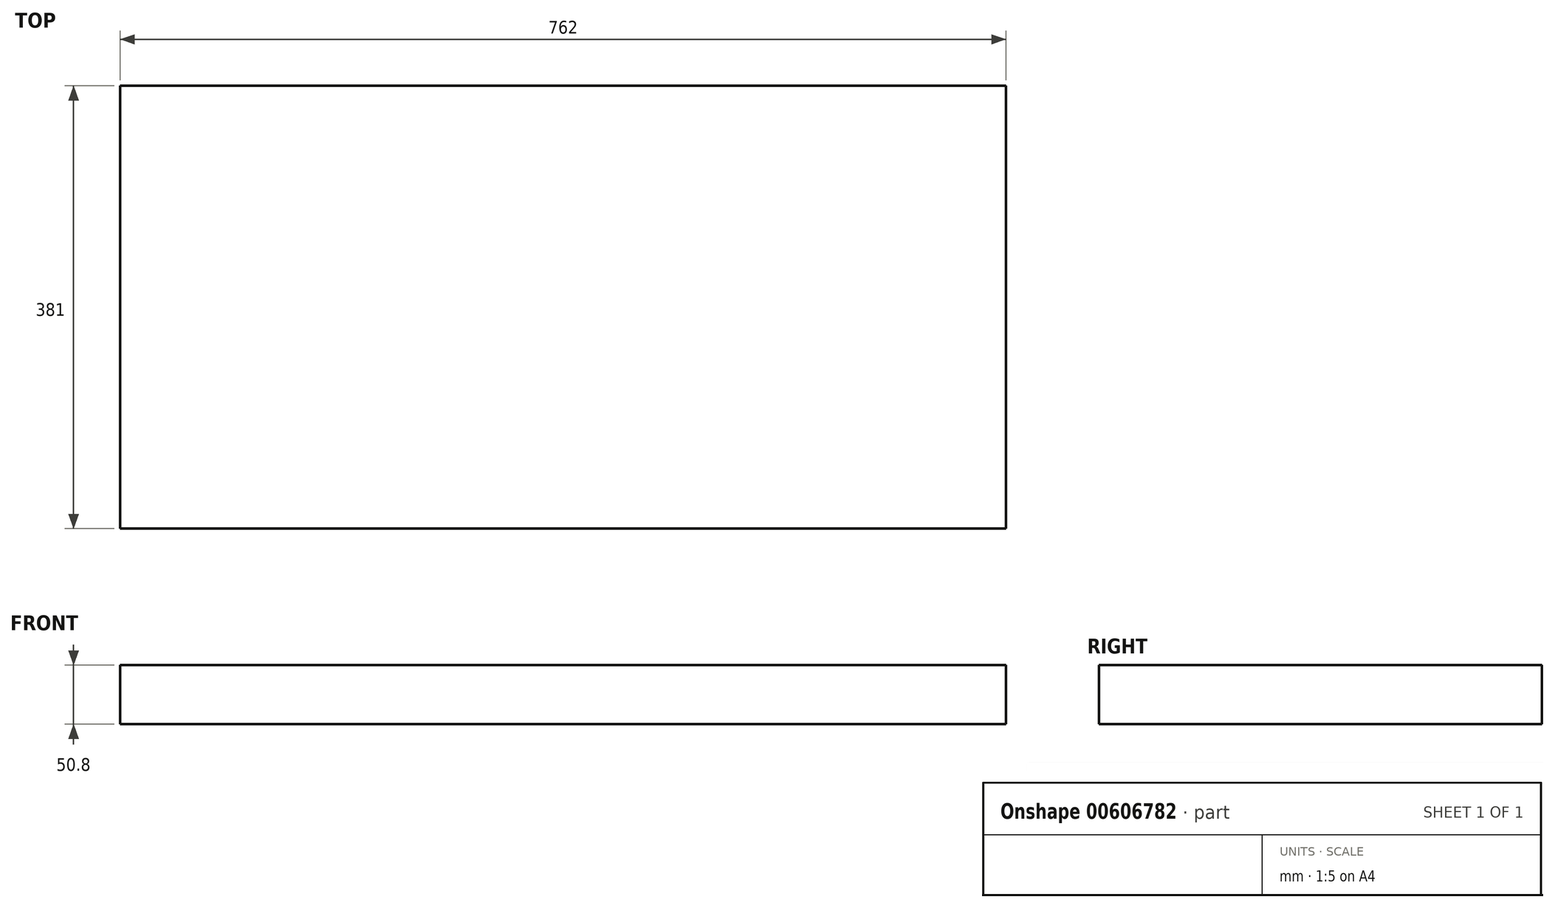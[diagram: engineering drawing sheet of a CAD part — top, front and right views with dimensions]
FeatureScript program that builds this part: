
annotation { "Feature Type Name" : "Feature", "Feature Type Description" : "" }
export const myFeature = defineFeature(function(context is Context, id is Id, definition is map)
    precondition{}
    {
        {
            var Q0;
            Q0=qCreatedBy(makeId("Top.planeOp"),FACE);
            var sketch = newSketch(context, id + "F0", { "sketchPlane" : qUnion([Q0])});
            skLineSegment(sketch, "E0.bottom", {"start": v(-383.35, -353.26) * mm, "end": v(378.65, -353.26) * mm});
            skLineSegment(sketch, "E0.top", {"start": v(-383.35, 27.74) * mm, "end": v(378.65, 27.74) * mm});
            skLineSegment(sketch, "E0.left", {"start": v(-383.35, -353.26) * mm, "end": v(-383.35, 27.74) * mm});
            skLineSegment(sketch, "E0.right", {"start": v(378.65, -353.26) * mm, "end": v(378.65, 27.74) * mm});
            skSolve(sketch);
        }
        {
            var Q0;
            Q0 = qSketchRegion(id + "F0", true);
            extrude(context, id + "F1", {"entities" : qUnion([Q0]), "depth" : 50.8 * mm, "offsetDistance" : 25.4 * mm});
        }
    });
